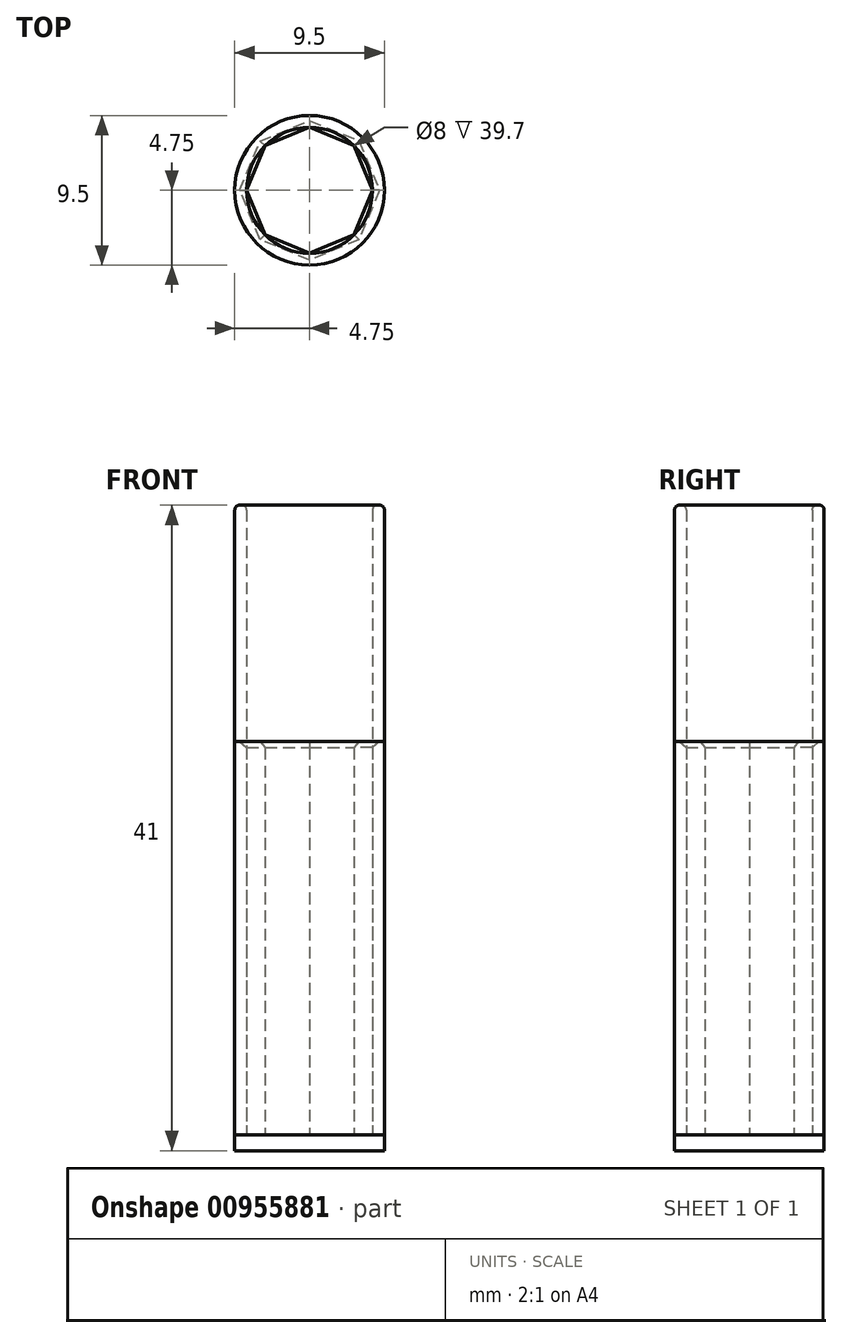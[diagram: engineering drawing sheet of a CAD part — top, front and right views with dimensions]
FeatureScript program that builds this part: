
annotation { "Feature Type Name" : "Feature", "Feature Type Description" : "" }
export const myFeature = defineFeature(function(context is Context, id is Id, definition is map)
    precondition{}
    {
        {
            var Q0;
            Q0=qCreatedBy(makeId("Top.planeOp"),FACE);
            var sketch = newSketch(context, id + "F0", { "sketchPlane" : qUnion([Q0])});
            skCircle(sketch, "E0", {"center": v(0, 0) * mm, "radius": 4 * mm});
            skCircle(sketch, "E1.cCircle", {"center": v(0, 0) * mm, "radius": 4 * mm, "construction": true});
            skLineSegment(sketch, "E1.0", {"start": v(0, -4) * mm, "end": v(-2.83, -2.83) * mm});
            skLineSegment(sketch, "E1.1", {"start": v(-2.83, -2.83) * mm, "end": v(-4, 0) * mm});
            skLineSegment(sketch, "E1.2", {"start": v(-4, 0) * mm, "end": v(-2.83, 2.83) * mm});
            skLineSegment(sketch, "E1.3", {"start": v(-2.83, 2.83) * mm, "end": v(0, 4) * mm});
            skLineSegment(sketch, "E1.4", {"start": v(0, 4) * mm, "end": v(2.83, 2.83) * mm});
            skLineSegment(sketch, "E1.5", {"start": v(2.83, 2.83) * mm, "end": v(4, 0) * mm});
            skLineSegment(sketch, "E1.6", {"start": v(4, 0) * mm, "end": v(2.83, -2.83) * mm});
            skLineSegment(sketch, "E1.7", {"start": v(2.83, -2.83) * mm, "end": v(0, -4) * mm});
            skCircle(sketch, "E2", {"center": v(0, 0) * mm, "radius": 4.75 * mm});
            skSolve(sketch);
        }
        {
            var Q0;
            Q0=makeQuery(id+"F0.imprint","IMPRINT",FACE,{"disambiguationData":[TD([[makeQuery(id+"F0.imprint","IMPRINT",EDGE,{"derivedFrom":sQuery(id+"F0.wireOp",EDGE,"E2")}),1.0]])]});
            var Q1;
            {var subQ0=sQuery(id+"F0.wireOp",EDGE,"E1.7");Q1=makeQuery(id+"F0.imprint","IMPRINT",FACE,{"disambiguationData":[TD([[makeQuery(id+"F0.imprint","IMPRINT",EDGE,{"derivedFrom":subQ0}),1.0]])]});}
            var Q2;
            {var subQ0=sQuery(id+"F0.wireOp",EDGE,"E1.6");Q2=makeQuery(id+"F0.imprint","IMPRINT",FACE,{"disambiguationData":[TD([[makeQuery(id+"F0.imprint","IMPRINT",EDGE,{"derivedFrom":subQ0}),1.0]])]});}
            var Q3;
            {var subQ0=sQuery(id+"F0.wireOp",EDGE,"E1.5");Q3=makeQuery(id+"F0.imprint","IMPRINT",FACE,{"disambiguationData":[TD([[makeQuery(id+"F0.imprint","IMPRINT",EDGE,{"derivedFrom":subQ0}),1.0]])]});}
            var Q4;
            {var subQ0=sQuery(id+"F0.wireOp",EDGE,"E1.4");Q4=makeQuery(id+"F0.imprint","IMPRINT",FACE,{"disambiguationData":[TD([[makeQuery(id+"F0.imprint","IMPRINT",EDGE,{"derivedFrom":subQ0}),1.0]])]});}
            var Q5;
            {var subQ0=sQuery(id+"F0.wireOp",EDGE,"E1.3");Q5=makeQuery(id+"F0.imprint","IMPRINT",FACE,{"disambiguationData":[TD([[makeQuery(id+"F0.imprint","IMPRINT",EDGE,{"derivedFrom":subQ0}),1.0]])]});}
            var Q6;
            {var subQ0=sQuery(id+"F0.wireOp",EDGE,"E1.2");Q6=makeQuery(id+"F0.imprint","IMPRINT",FACE,{"disambiguationData":[TD([[makeQuery(id+"F0.imprint","IMPRINT",EDGE,{"derivedFrom":subQ0}),1.0]])]});}
            var Q7;
            {var subQ0=sQuery(id+"F0.wireOp",EDGE,"E1.1");Q7=makeQuery(id+"F0.imprint","IMPRINT",FACE,{"disambiguationData":[TD([[makeQuery(id+"F0.imprint","IMPRINT",EDGE,{"derivedFrom":subQ0}),1.0]])]});}
            var Q8;
            {var subQ0=sQuery(id+"F0.wireOp",EDGE,"E1.0");Q8=makeQuery(id+"F0.imprint","IMPRINT",FACE,{"disambiguationData":[TD([[makeQuery(id+"F0.imprint","IMPRINT",EDGE,{"derivedFrom":subQ0}),1.0]])]});}
            extrude(context, id + "F1", {"entities" : qUnion([Q0, Q1, Q2, Q3, Q4, Q5, Q6, Q7, Q8]), "depth" : 25 * mm, "offsetDistance" : 25 * mm});
        }
        {
            var Q0;
            Q0=makeQuery(id+"F0.imprint","IMPRINT",FACE,{"disambiguationData":[TD([[makeQuery(id+"F0.imprint","IMPRINT",EDGE,{"derivedFrom":sQuery(id+"F0.wireOp",EDGE,"E2")}),1.0]])]});
            extrude(context, id + "F2", {"entities" : qUnion([Q0]), "depth" : 40 * mm, "offsetDistance" : 25 * mm});
        }
        {
            var Q0;
            Q0=makeQuery(id+"F0.imprint","IMPRINT",FACE,{"disambiguationData":[TD([[makeQuery(id+"F0.imprint","IMPRINT",EDGE,{"derivedFrom":sQuery(id+"F0.wireOp",EDGE,"E2")}),1.0]])]});
            var Q1;
            {var subQ0=sQuery(id+"F0.wireOp",EDGE,"E1.4");Q1=makeQuery(id+"F0.imprint","IMPRINT",FACE,{"disambiguationData":[TD([[makeQuery(id+"F0.imprint","IMPRINT",EDGE,{"derivedFrom":subQ0}),1.0]])]});}
            var Q2;
            {var subQ0=sQuery(id+"F0.wireOp",EDGE,"E1.5");Q2=makeQuery(id+"F0.imprint","IMPRINT",FACE,{"disambiguationData":[TD([[makeQuery(id+"F0.imprint","IMPRINT",EDGE,{"derivedFrom":subQ0}),1.0]])]});}
            var Q3;
            {var subQ0=sQuery(id+"F0.wireOp",EDGE,"E1.3");Q3=makeQuery(id+"F0.imprint","IMPRINT",FACE,{"disambiguationData":[TD([[makeQuery(id+"F0.imprint","IMPRINT",EDGE,{"derivedFrom":subQ0}),1.0]])]});}
            var Q4;
            {var subQ0=sQuery(id+"F0.wireOp",EDGE,"E1.2");Q4=makeQuery(id+"F0.imprint","IMPRINT",FACE,{"disambiguationData":[TD([[makeQuery(id+"F0.imprint","IMPRINT",EDGE,{"derivedFrom":subQ0}),1.0]])]});}
            var Q5;
            {var subQ0=sQuery(id+"F0.wireOp",EDGE,"E1.6");Q5=makeQuery(id+"F0.imprint","IMPRINT",FACE,{"disambiguationData":[TD([[makeQuery(id+"F0.imprint","IMPRINT",EDGE,{"derivedFrom":subQ0}),1.0]])]});}
            var Q6;
            {var subQ0=sQuery(id+"F0.wireOp",EDGE,"E1.7");Q6=makeQuery(id+"F0.imprint","IMPRINT",FACE,{"disambiguationData":[TD([[makeQuery(id+"F0.imprint","IMPRINT",EDGE,{"derivedFrom":subQ0}),1.0]])]});}
            var Q7;
            {var subQ0=sQuery(id+"F0.wireOp",EDGE,"E1.0");Q7=makeQuery(id+"F0.imprint","IMPRINT",FACE,{"disambiguationData":[TD([[makeQuery(id+"F0.imprint","IMPRINT",EDGE,{"derivedFrom":subQ0}),1.0]])]});}
            var Q8;
            {var subQ0=sQuery(id+"F0.wireOp",EDGE,"E1.1");Q8=makeQuery(id+"F0.imprint","IMPRINT",FACE,{"disambiguationData":[TD([[makeQuery(id+"F0.imprint","IMPRINT",EDGE,{"derivedFrom":subQ0}),1.0]])]});}
            var Q9;
            Q9=makeQuery(id+"F0.imprint","IMPRINT",FACE,{"disambiguationData":[TD([[makeQuery(id+"F0.imprint","IMPRINT",EDGE,{"derivedFrom":sQuery(id+"F0.wireOp",EDGE,"E1.0")}),-1.0]])]});
            extrude(context, id + "F3", {"entities" : qUnion([Q0, Q1, Q2, Q3, Q4, Q5, Q6, Q7, Q8, Q9]), "oppositeDirection" : true, "depth" : 1 * mm, "offsetDistance" : 25 * mm});
        }
        {
            var Q0;
            Q0=makeQuery(id+"F2.opExtrude","CAP_FACE",FACE,{"disambiguationData":[OSD([sQuery(id+"F0.wireOp",EDGE,"E0"),sQuery(id+"F0.wireOp",EDGE,"E2")])],"isStart":false});
            fillet(context, id + "F4", {"entities" : qUnion([Q0]), "radius" : 0.3 * mm, "tangentPropagation" : true, "allowEdgeOverflow" : false});
        }
        {
            var Q0;
            Q0=makeQuery(id+"F1.opExtrude","CAP_EDGE",EDGE,{"disambiguationData":[OSD([sQuery(id+"F0.wireOp",EDGE,"E1.1")])],"isStart":false});
            var Q1;
            Q1=makeQuery(id+"F1.opExtrude","CAP_EDGE",EDGE,{"disambiguationData":[OSD([sQuery(id+"F0.wireOp",EDGE,"E1.2")])],"isStart":false});
            var Q2;
            Q2=makeQuery(id+"F1.opExtrude","CAP_EDGE",EDGE,{"disambiguationData":[OSD([sQuery(id+"F0.wireOp",EDGE,"E1.3")])],"isStart":false});
            var Q3;
            Q3=makeQuery(id+"F1.opExtrude","CAP_EDGE",EDGE,{"disambiguationData":[OSD([sQuery(id+"F0.wireOp",EDGE,"E1.4")])],"isStart":false});
            var Q4;
            Q4=makeQuery(id+"F1.opExtrude","CAP_EDGE",EDGE,{"disambiguationData":[OSD([sQuery(id+"F0.wireOp",EDGE,"E1.5")])],"isStart":false});
            var Q5;
            Q5=makeQuery(id+"F1.opExtrude","CAP_EDGE",EDGE,{"disambiguationData":[OSD([sQuery(id+"F0.wireOp",EDGE,"E1.6")])],"isStart":false});
            var Q6;
            Q6=makeQuery(id+"F1.opExtrude","CAP_EDGE",EDGE,{"disambiguationData":[OSD([sQuery(id+"F0.wireOp",EDGE,"E1.7")])],"isStart":false});
            var Q7;
            Q7=makeQuery(id+"F1.opExtrude","CAP_EDGE",EDGE,{"disambiguationData":[OSD([sQuery(id+"F0.wireOp",EDGE,"E1.0")])],"isStart":false});
            chamfer(context, id + "F5", {"entities" : qUnion([Q0, Q1, Q2, Q3, Q4, Q5, Q6, Q7]), "width" : 0.4 * mm, "tangentPropagation" : true});
        }
    });
